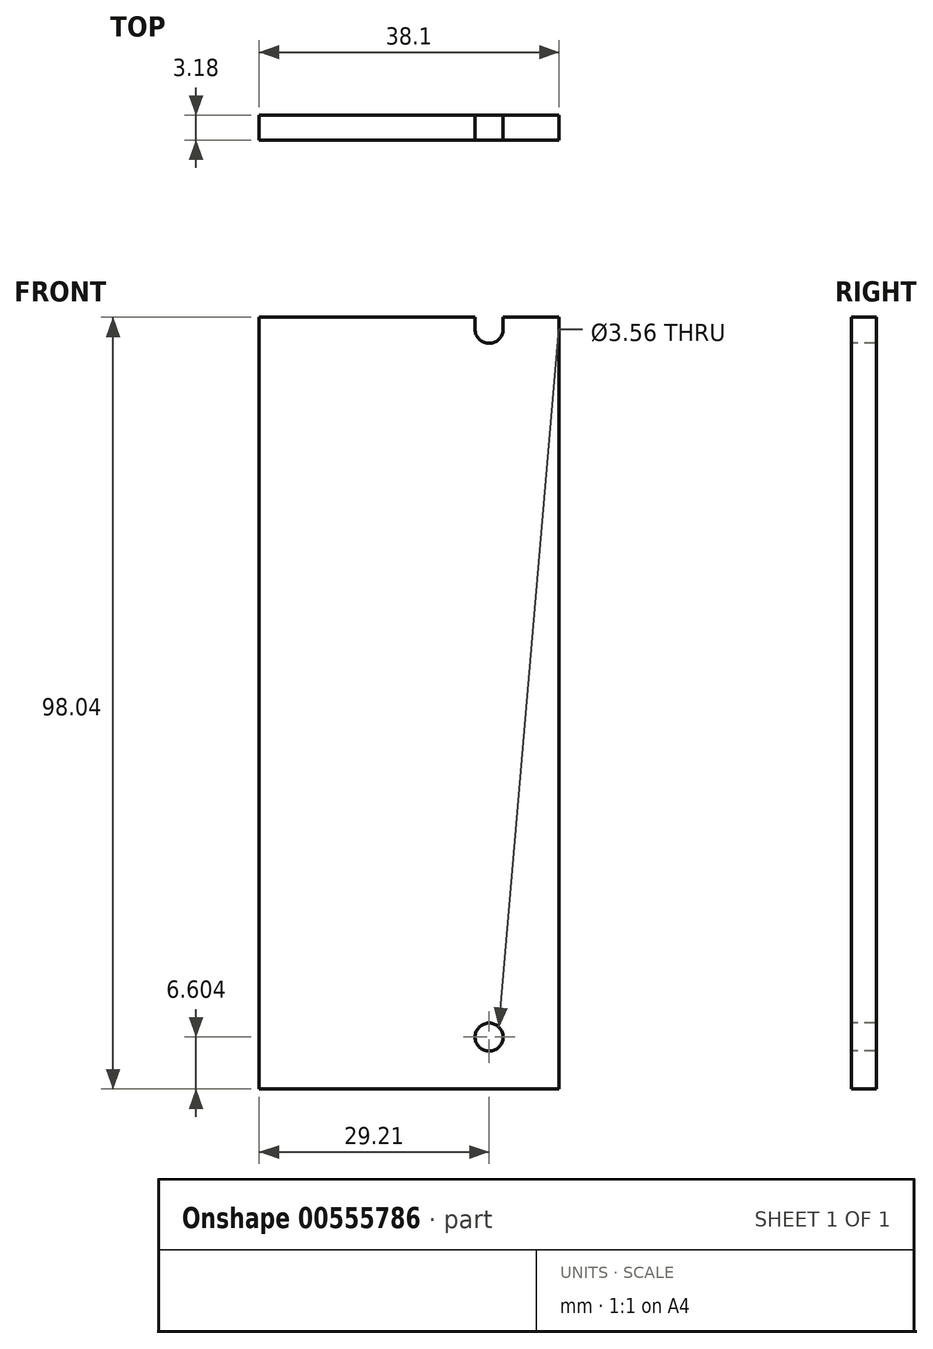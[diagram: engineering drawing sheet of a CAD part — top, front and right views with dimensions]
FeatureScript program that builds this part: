
annotation { "Feature Type Name" : "Feature", "Feature Type Description" : "" }
export const myFeature = defineFeature(function(context is Context, id is Id, definition is map)
    precondition{}
    {
        {
            var Q0;
            Q0=qCreatedBy(makeId("Front.planeOp"),FACE);
            var sketch = newSketch(context, id + "F0", { "sketchPlane" : qUnion([Q0])});
            skLineSegment(sketch, "E0.bottom", {"start": v(-38.1, 98.04) * mm, "end": v(0, 98.04) * mm});
            skLineSegment(sketch, "E0.top", {"start": v(-38.1, 0) * mm, "end": v(0, 0) * mm});
            skLineSegment(sketch, "E0.left", {"start": v(-38.1, 98.04) * mm, "end": v(-38.1, 0) * mm});
            skLineSegment(sketch, "E0.right", {"start": v(0, 98.04) * mm, "end": v(0, 0) * mm});
            skSolve(sketch);
        }
        {
            var Q0;
            Q0=makeQuery(id+"F0.imprint","IMPRINT",FACE,{"disambiguationData":[TD([[makeQuery(id+"F0.imprint","IMPRINT",EDGE,{"derivedFrom":sQuery(id+"F0.wireOp",EDGE,"E0.bottom")}),-1.0]])]});
            extrude(context, id + "F1", {"entities" : qUnion([Q0]), "depth" : 3.17 * mm, "offsetDistance" : 25.4 * mm});
        }
        {
            var Q0;
            Q0=makeQuery(id+"F1.opExtrude","CAP_FACE",FACE,{"disambiguationData":[OSD([sQuery(id+"F0.wireOp",EDGE,"E0.bottom"),sQuery(id+"F0.wireOp",EDGE,"E0.top"),sQuery(id+"F0.wireOp",EDGE,"E0.left"),sQuery(id+"F0.wireOp",EDGE,"E0.right")])],"isStart":false});
            var sketch = newSketch(context, id + "F2", { "sketchPlane" : qUnion([Q0])});
            skCircle(sketch, "E1", {"center": v(-8.89, 6.6) * mm, "radius": 1.78 * mm});
            skLineSegment(sketch, "E2", {"start": v(-7.11, 96.52) * mm, "end": v(-7.11, 98.04) * mm});
            skLineSegment(sketch, "E3", {"start": v(-10.67, 96.52) * mm, "end": v(-10.67, 98.04) * mm});
            skLineSegment(sketch, "E4", {"start": v(-7.11, 98.04) * mm, "end": v(-10.67, 98.04) * mm});
            skArc(sketch, "E5", {"start": v(-10.67, 96.52) * mm, "mid": v(-8.9, 94.74) * mm, "end": v(-7.11, 96.52) * mm});
            skSolve(sketch);
        }
        {
            var Q0;
            Q0 = qSketchRegion(id + "F2", true);
            extrude(context, id + "F3", {"entities" : qUnion([Q0]), "operationType" : NewBodyOperationType.REMOVE, "endBound" : BoundingType.THROUGH_ALL, "oppositeDirection" : true, "depth" : 25.4 * mm, "offsetDistance" : 25.4 * mm});
        }
    });
